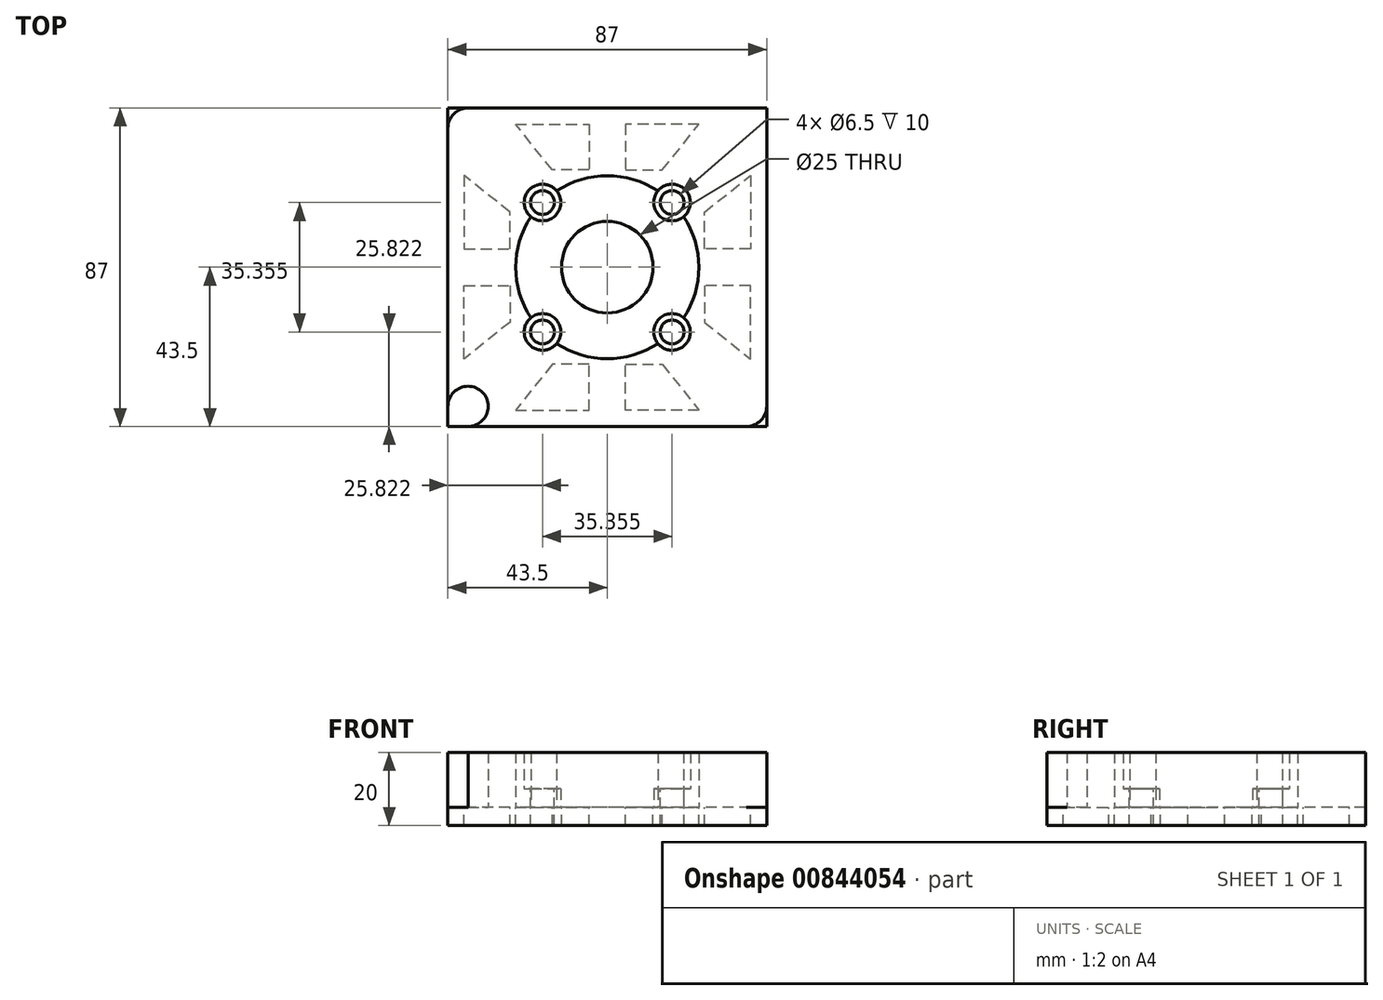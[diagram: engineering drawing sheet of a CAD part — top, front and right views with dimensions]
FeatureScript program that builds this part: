
annotation { "Feature Type Name" : "Feature", "Feature Type Description" : "" }
export const myFeature = defineFeature(function(context is Context, id is Id, definition is map)
    precondition{}
    {
        {
            var Q0;
            Q0=qCreatedBy(makeId("Top.planeOp"),FACE);
            var sketch = newSketch(context, id + "F0", { "sketchPlane" : qUnion([Q0])});
            skLineSegment(sketch, "E0.bottom", {"start": v(-43.5, 43.5) * mm, "end": v(43.5, 43.5) * mm});
            skLineSegment(sketch, "E0.top", {"start": v(-43.5, -43.5) * mm, "end": v(43.5, -43.5) * mm});
            skLineSegment(sketch, "E0.left", {"start": v(-43.5, 43.5) * mm, "end": v(-43.5, -43.5) * mm});
            skLineSegment(sketch, "E0.right", {"start": v(43.5, 43.5) * mm, "end": v(43.5, -43.5) * mm});
            skPoint(sketch, "E0.middle", {"position": v(0, 0) * mm});
            skSolve(sketch);
        }
        {
            var Q0;
            Q0=makeQuery(id+"F0.imprint","IMPRINT",FACE,{"disambiguationData":[TD([[makeQuery(id+"F0.imprint","IMPRINT",EDGE,{"derivedFrom":sQuery(id+"F0.wireOp",EDGE,"E0.bottom")}),-1.0]])]});
            extrude(context, id + "F1", {"entities" : qUnion([Q0]), "depth" : 5 * mm, "offsetDistance" : 25 * mm});
        }
        {
            var Q0;
            Q0=makeQuery(id+"F1.opExtrude","CAP_FACE",FACE,{"disambiguationData":[OSD([sQuery(id+"F0.wireOp",EDGE,"E0.bottom"),sQuery(id+"F0.wireOp",EDGE,"E0.top"),sQuery(id+"F0.wireOp",EDGE,"E0.left"),sQuery(id+"F0.wireOp",EDGE,"E0.right")])],"isStart":false});
            var sketch = newSketch(context, id + "F2", { "sketchPlane" : qUnion([Q0])});
            skCircle(sketch, "E1", {"center": v(0, 0) * mm, "radius": 25 * mm});
            skLineSegment(sketch, "E2", {"start": v(0, 0) * mm, "end": v(-17.68, 17.68) * mm});
            skLineSegment(sketch, "E3", {"start": v(0, 0) * mm, "end": v(17.68, 17.68) * mm});
            skLineSegment(sketch, "E4", {"start": v(0, 0) * mm, "end": v(17.68, -17.68) * mm});
            skLineSegment(sketch, "E5", {"start": v(0, 0) * mm, "end": v(-17.68, -17.68) * mm});
            skPoint(sketch, "E6", {"position": v(-17.68, 17.68) * mm});
            skPoint(sketch, "E7", {"position": v(-17.68, -17.68) * mm});
            skPoint(sketch, "E8", {"position": v(17.68, -17.68) * mm});
            skPoint(sketch, "E9", {"position": v(17.68, 17.68) * mm});
            skCircle(sketch, "E10", {"center": v(-17.68, 17.68) * mm, "radius": 5 * mm});
            skCircle(sketch, "E11", {"center": v(17.68, 17.68) * mm, "radius": 5 * mm});
            skCircle(sketch, "E12", {"center": v(17.68, -17.68) * mm, "radius": 5 * mm});
            skCircle(sketch, "E13", {"center": v(-17.68, -17.68) * mm, "radius": 5 * mm});
            skSolve(sketch);
        }
        {
            var Q0;
            {var subQ0=sQuery(id+"F2.wireOp",EDGE,"E1");var subQ1=makeQuery(id+"F2.imprint","INTERSECT",VERTEX,{"derivedFrom":[subQ0,sQuery(id+"F2.wireOp",EDGE,"E2")]});Q0=makeQuery(id+"F2.imprint","IMPRINT",FACE,{"disambiguationData":[TD([[makeQuery(id+"F2.imprint","IMPRINT",EDGE,{"disambiguationData":[TD([[subQ1,1.0]])],"derivedFrom":subQ0}),-1.0]])]});}
            var Q1;
            {var subQ0=sQuery(id+"F2.wireOp",EDGE,"E2");var subQ1=sQuery(id+"F2.wireOp",EDGE,"E1");var subQ2=makeQuery(id+"F2.imprint","INTERSECT",VERTEX,{"derivedFrom":[subQ1,subQ0]});Q1=makeQuery(id+"F2.imprint","IMPRINT",FACE,{"disambiguationData":[TD([[makeQuery(id+"F2.imprint","IMPRINT",EDGE,{"disambiguationData":[TD([[subQ2,1.0]])],"derivedFrom":subQ1}),1.0]])]});}
            var Q2;
            {var subQ0=sQuery(id+"F2.wireOp",EDGE,"E2");var subQ1=sQuery(id+"F2.wireOp",EDGE,"E1");var subQ2=makeQuery(id+"F2.imprint","INTERSECT",VERTEX,{"derivedFrom":[subQ1,subQ0]});Q2=makeQuery(id+"F2.imprint","IMPRINT",FACE,{"disambiguationData":[TD([[makeQuery(id+"F2.imprint","IMPRINT",EDGE,{"disambiguationData":[TD([[subQ2,-1.0]])],"derivedFrom":subQ1}),1.0]])]});}
            var Q3;
            {var subQ0=sQuery(id+"F2.wireOp",EDGE,"E5");var subQ1=sQuery(id+"F2.wireOp",EDGE,"E1");var subQ2=makeQuery(id+"F2.imprint","INTERSECT",VERTEX,{"derivedFrom":[subQ1,subQ0]});Q3=makeQuery(id+"F2.imprint","IMPRINT",FACE,{"disambiguationData":[TD([[makeQuery(id+"F2.imprint","IMPRINT",EDGE,{"disambiguationData":[TD([[subQ2,1.0]])],"derivedFrom":subQ1}),1.0]])]});}
            var Q4;
            {var subQ0=sQuery(id+"F2.wireOp",EDGE,"E5");var subQ1=sQuery(id+"F2.wireOp",EDGE,"E1");var subQ2=makeQuery(id+"F2.imprint","INTERSECT",VERTEX,{"derivedFrom":[subQ1,subQ0]});Q4=makeQuery(id+"F2.imprint","IMPRINT",FACE,{"disambiguationData":[TD([[makeQuery(id+"F2.imprint","IMPRINT",EDGE,{"disambiguationData":[TD([[subQ2,-1.0]])],"derivedFrom":subQ1}),1.0]])]});}
            var Q5;
            {var subQ0=sQuery(id+"F2.wireOp",EDGE,"E1");var subQ1=makeQuery(id+"F2.imprint","INTERSECT",VERTEX,{"derivedFrom":[subQ0,sQuery(id+"F2.wireOp",EDGE,"E5")]});Q5=makeQuery(id+"F2.imprint","IMPRINT",FACE,{"disambiguationData":[TD([[makeQuery(id+"F2.imprint","IMPRINT",EDGE,{"disambiguationData":[TD([[subQ1,1.0]])],"derivedFrom":subQ0}),-1.0]])]});}
            var Q6;
            {var subQ0=sQuery(id+"F2.wireOp",EDGE,"E4");var subQ1=sQuery(id+"F2.wireOp",EDGE,"E1");var subQ2=makeQuery(id+"F2.imprint","INTERSECT",VERTEX,{"derivedFrom":[subQ1,subQ0]});Q6=makeQuery(id+"F2.imprint","IMPRINT",FACE,{"disambiguationData":[TD([[makeQuery(id+"F2.imprint","IMPRINT",EDGE,{"disambiguationData":[TD([[subQ2,-1.0]])],"derivedFrom":subQ1}),1.0]])]});}
            var Q7;
            {var subQ0=sQuery(id+"F2.wireOp",EDGE,"E4");var subQ1=sQuery(id+"F2.wireOp",EDGE,"E1");var subQ2=makeQuery(id+"F2.imprint","INTERSECT",VERTEX,{"derivedFrom":[subQ1,subQ0]});Q7=makeQuery(id+"F2.imprint","IMPRINT",FACE,{"disambiguationData":[TD([[makeQuery(id+"F2.imprint","IMPRINT",EDGE,{"disambiguationData":[TD([[subQ2,1.0]])],"derivedFrom":subQ1}),1.0]])]});}
            var Q8;
            {var subQ0=sQuery(id+"F2.wireOp",EDGE,"E1");var subQ1=makeQuery(id+"F2.imprint","INTERSECT",VERTEX,{"derivedFrom":[subQ0,sQuery(id+"F2.wireOp",EDGE,"E4")]});Q8=makeQuery(id+"F2.imprint","IMPRINT",FACE,{"disambiguationData":[TD([[makeQuery(id+"F2.imprint","IMPRINT",EDGE,{"disambiguationData":[TD([[subQ1,1.0]])],"derivedFrom":subQ0}),-1.0]])]});}
            var Q9;
            {var subQ0=sQuery(id+"F2.wireOp",EDGE,"E1");var subQ1=makeQuery(id+"F2.imprint","INTERSECT",VERTEX,{"derivedFrom":[subQ0,sQuery(id+"F2.wireOp",EDGE,"E3")]});Q9=makeQuery(id+"F2.imprint","IMPRINT",FACE,{"disambiguationData":[TD([[makeQuery(id+"F2.imprint","IMPRINT",EDGE,{"disambiguationData":[TD([[subQ1,1.0]])],"derivedFrom":subQ0}),-1.0]])]});}
            var Q10;
            {var subQ0=sQuery(id+"F2.wireOp",EDGE,"E3");var subQ1=sQuery(id+"F2.wireOp",EDGE,"E1");var subQ2=makeQuery(id+"F2.imprint","INTERSECT",VERTEX,{"derivedFrom":[subQ1,subQ0]});Q10=makeQuery(id+"F2.imprint","IMPRINT",FACE,{"disambiguationData":[TD([[makeQuery(id+"F2.imprint","IMPRINT",EDGE,{"disambiguationData":[TD([[subQ2,-1.0]])],"derivedFrom":subQ1}),1.0]])]});}
            var Q11;
            {var subQ0=sQuery(id+"F2.wireOp",EDGE,"E3");var subQ1=sQuery(id+"F2.wireOp",EDGE,"E1");var subQ2=makeQuery(id+"F2.imprint","INTERSECT",VERTEX,{"derivedFrom":[subQ1,subQ0]});Q11=makeQuery(id+"F2.imprint","IMPRINT",FACE,{"disambiguationData":[TD([[makeQuery(id+"F2.imprint","IMPRINT",EDGE,{"disambiguationData":[TD([[subQ2,1.0]])],"derivedFrom":subQ1}),1.0]])]});}
            extrude(context, id + "F3", {"entities" : qUnion([Q0, Q1, Q2, Q3, Q4, Q5, Q6, Q7, Q8, Q9, Q10, Q11]), "operationType" : NewBodyOperationType.ADD, "depth" : 5 * mm, "offsetDistance" : 25 * mm});
        }
        {
            var Q0;
            Q0=makeQuery(id+"F2.imprint","IMPRINT",FACE,{"disambiguationData":[TD([[makeQuery(id+"F2.imprint","IMPRINT",EDGE,{"derivedFrom":makeQuery(id+"F1.opExtrude","CAP_EDGE",EDGE,{"disambiguationData":[OSD([sQuery(id+"F0.wireOp",EDGE,"E0.bottom")])],"isStart":false})}),-1.0]])]});
            cPlane(context, id + "F4", {"entities" : qUnion([Q0]), "cplaneType" : CPlaneType.OFFSET, "offset" : 5 * mm, "width" : 150 * mm, "height" : 150 * mm});
        }
        {
            var Q0;
            Q0=qCreatedBy(id+"F4.planeOp",FACE);
            var sketch = newSketch(context, id + "F5", { "sketchPlane" : qUnion([Q0])});
            skCircle(sketch, "E14", {"center": v(0, 0) * mm, "radius": 25 * mm});
            skLineSegment(sketch, "E15", {"start": v(0, 0) * mm, "end": v(-17.68, 17.68) * mm});
            skLineSegment(sketch, "E16", {"start": v(0, 0) * mm, "end": v(17.68, 17.68) * mm});
            skLineSegment(sketch, "E17", {"start": v(0, 0) * mm, "end": v(17.68, -17.68) * mm});
            skLineSegment(sketch, "E18", {"start": v(0, 0) * mm, "end": v(-17.68, -17.68) * mm});
            skPoint(sketch, "E19", {"position": v(-17.68, 17.68) * mm});
            skPoint(sketch, "E20", {"position": v(-17.68, -17.68) * mm});
            skPoint(sketch, "E21", {"position": v(17.68, -17.68) * mm});
            skPoint(sketch, "E22", {"position": v(17.68, 17.68) * mm});
            skCircle(sketch, "E23", {"center": v(-17.68, 17.68) * mm, "radius": 5 * mm});
            skCircle(sketch, "E24", {"center": v(17.68, 17.68) * mm, "radius": 5 * mm});
            skCircle(sketch, "E25", {"center": v(17.68, -17.68) * mm, "radius": 5 * mm});
            skCircle(sketch, "E26", {"center": v(-17.68, -17.68) * mm, "radius": 5 * mm});
            skSolve(sketch);
        }
        {
            var Q0;
            Q0=sQuery(id+"F5.wireOp",VERTEX,"E19");
            var Q1;
            Q1=sQuery(id+"F5.wireOp",VERTEX,"E22");
            var Q2;
            Q2=sQuery(id+"F5.wireOp",VERTEX,"E21");
            var Q3;
            Q3=sQuery(id+"F5.wireOp",VERTEX,"E20");
            var Q4;
            Q4=makeQuery(id+"F1.opExtrude","SWEPT_BODY",BODY,{"disambiguationData":[OSD([sQuery(id+"F0.wireOp",EDGE,"E0.bottom"),sQuery(id+"F0.wireOp",EDGE,"E0.top"),sQuery(id+"F0.wireOp",EDGE,"E0.left"),sQuery(id+"F0.wireOp",EDGE,"E0.right")])]});
            hole(context, id + "F6", {"style" : HoleStyle.SIMPLE, "endStyle" : HoleEndStyle.THROUGH, "holeDiameter" : 6.5 * mm, "majorDiameter" : 5 * mm, "isTappedThrough" : true, "tappedDepth" : 12 * mm, "tapClearance" : 3, "locations" : qUnion([Q0, Q1, Q2, Q3]), "scope" : qUnion([Q4])});
        }
        {
            var Q0;
            Q0=makeQuery(id+"F2.imprint","IMPRINT",FACE,{"disambiguationData":[TD([[makeQuery(id+"F2.imprint","IMPRINT",EDGE,{"derivedFrom":makeQuery(id+"F1.opExtrude","CAP_EDGE",EDGE,{"disambiguationData":[OSD([sQuery(id+"F0.wireOp",EDGE,"E0.bottom")])],"isStart":false})}),-1.0]])]});
            var sketch = newSketch(context, id + "F7", { "sketchPlane" : qUnion([Q0])});
            skCircle(sketch, "E27", {"center": v(-38, 38) * mm, "radius": 5.5 * mm});
            skCircle(sketch, "E28.MirrorC", {"center": v(-38, -38) * mm, "radius": 5.5 * mm});
            skCircle(sketch, "E29.MirrorC", {"center": v(38, -38) * mm, "radius": 5.5 * mm});
            skSolve(sketch);
        }
        {
            var Q0;
            {var subQ0=sQuery(id+"F7.wireOp",EDGE,"E27");var subQ1=makeQuery(id+"F7.imprint","INTERSECT",VERTEX,{"derivedFrom":[makeQuery(id+"F2.imprint","IMPRINT",EDGE,{"derivedFrom":makeQuery(id+"F1.opExtrude","CAP_EDGE",EDGE,{"disambiguationData":[OSD([sQuery(id+"F0.wireOp",EDGE,"E0.bottom")])],"isStart":false})}),subQ0]});Q0=makeQuery(id+"F7.imprint","IMPRINT",FACE,{"disambiguationData":[TD([[makeQuery(id+"F7.imprint","IMPRINT",EDGE,{"disambiguationData":[TD([[subQ1,-1.0]])],"derivedFrom":subQ0}),1.0]])]});}
            var Q1;
            {var subQ0=sQuery(id+"F7.wireOp",EDGE,"E28.MirrorC");var subQ1=makeQuery(id+"F7.imprint","INTERSECT",VERTEX,{"derivedFrom":[makeQuery(id+"F2.imprint","IMPRINT",EDGE,{"derivedFrom":makeQuery(id+"F1.opExtrude","CAP_EDGE",EDGE,{"disambiguationData":[OSD([sQuery(id+"F0.wireOp",EDGE,"E0.top")])],"isStart":false})}),subQ0]});Q1=makeQuery(id+"F7.imprint","IMPRINT",FACE,{"disambiguationData":[TD([[makeQuery(id+"F7.imprint","IMPRINT",EDGE,{"disambiguationData":[TD([[subQ1,-1.0]])],"derivedFrom":subQ0}),-1.0]])]});}
            var Q2;
            {var subQ0=sQuery(id+"F7.wireOp",EDGE,"E29.MirrorC");var subQ1=makeQuery(id+"F7.imprint","INTERSECT",VERTEX,{"derivedFrom":[makeQuery(id+"F2.imprint","IMPRINT",EDGE,{"derivedFrom":makeQuery(id+"F1.opExtrude","CAP_EDGE",EDGE,{"disambiguationData":[OSD([sQuery(id+"F0.wireOp",EDGE,"E0.top")])],"isStart":false})}),subQ0]});Q2=makeQuery(id+"F7.imprint","IMPRINT",FACE,{"disambiguationData":[TD([[makeQuery(id+"F7.imprint","IMPRINT",EDGE,{"disambiguationData":[TD([[subQ1,-1.0]])],"derivedFrom":subQ0}),1.0]])]});}
            extrude(context, id + "F8", {"entities" : qUnion([Q0, Q1, Q2]), "operationType" : NewBodyOperationType.ADD, "depth" : 15 * mm, "offsetDistance" : 25 * mm});
        }
        {
            var Q0;
            Q0=makeQuery(id+"F2.imprint","IMPRINT",FACE,{"disambiguationData":[TD([[makeQuery(id+"F2.imprint","IMPRINT",EDGE,{"derivedFrom":makeQuery(id+"F1.opExtrude","CAP_EDGE",EDGE,{"disambiguationData":[OSD([sQuery(id+"F0.wireOp",EDGE,"E0.bottom")])],"isStart":false})}),-1.0]])]});
            var sketch = newSketch(context, id + "F9", { "sketchPlane" : qUnion([Q0])});
            skLineSegment(sketch, "E30", {"start": v(5.01, 26.55) * mm, "end": v(15.03, 26.55) * mm});
            skLineSegment(sketch, "E31", {"start": v(15.03, 26.55) * mm, "end": v(25.05, 39.08) * mm});
            skLineSegment(sketch, "E32", {"start": v(25.05, 39.08) * mm, "end": v(5.01, 39.08) * mm});
            skLineSegment(sketch, "E33", {"start": v(5.01, 39.08) * mm, "end": v(5.01, 26.55) * mm});
            skLineSegment(sketch, "E34.MirrorCS", {"start": v(-25.05, 39.08) * mm, "end": v(-5.01, 39.08) * mm});
            skLineSegment(sketch, "E35.MirrorCS", {"start": v(-5.01, 39.08) * mm, "end": v(-5.01, 26.55) * mm});
            skLineSegment(sketch, "E36.MirrorCS", {"start": v(-5.01, 26.55) * mm, "end": v(-15.03, 26.55) * mm});
            skLineSegment(sketch, "E37.MirrorCS", {"start": v(-15.03, 26.55) * mm, "end": v(-25.05, 39.08) * mm});
            skLineSegment(sketch, "E38.MirrorCS", {"start": v(26.55, 5.01) * mm, "end": v(26.55, 15.03) * mm});
            skLineSegment(sketch, "E39.MirrorCS", {"start": v(39.08, 5.01) * mm, "end": v(26.55, 5.01) * mm});
            skLineSegment(sketch, "E40.MirrorCS", {"start": v(39.08, 25.05) * mm, "end": v(39.08, 5.01) * mm});
            skLineSegment(sketch, "E41.MirrorCS", {"start": v(26.55, 15.03) * mm, "end": v(39.08, 25.05) * mm});
            skLineSegment(sketch, "E42.MirrorCS", {"start": v(26.55, -5.01) * mm, "end": v(26.55, -15.03) * mm});
            skLineSegment(sketch, "E43.MirrorCS", {"start": v(39.08, -5.01) * mm, "end": v(26.55, -5.01) * mm});
            skLineSegment(sketch, "E44.MirrorCS", {"start": v(39.08, -25.05) * mm, "end": v(39.08, -5.01) * mm});
            skLineSegment(sketch, "E45.MirrorCS", {"start": v(26.55, -15.03) * mm, "end": v(39.08, -25.05) * mm});
            skLineSegment(sketch, "E46.MirrorCS", {"start": v(-25.05, -39.08) * mm, "end": v(-5.01, -39.08) * mm});
            skLineSegment(sketch, "E47.MirrorCS", {"start": v(-5.01, -39.08) * mm, "end": v(-5.01, -26.55) * mm});
            skLineSegment(sketch, "E48.MirrorCS", {"start": v(5.01, -39.08) * mm, "end": v(5.01, -26.55) * mm});
            skLineSegment(sketch, "E49.MirrorCS", {"start": v(-15.03, -26.55) * mm, "end": v(-25.05, -39.08) * mm});
            skLineSegment(sketch, "E50.MirrorCS", {"start": v(25.05, -39.08) * mm, "end": v(5.01, -39.08) * mm});
            skLineSegment(sketch, "E51.MirrorCS", {"start": v(5.01, -26.55) * mm, "end": v(15.03, -26.55) * mm});
            skLineSegment(sketch, "E52.MirrorCS", {"start": v(15.03, -26.55) * mm, "end": v(25.05, -39.08) * mm});
            skLineSegment(sketch, "E53.MirrorCS", {"start": v(-5.01, -26.55) * mm, "end": v(-15.03, -26.55) * mm});
            skLineSegment(sketch, "E54.MirrorCS", {"start": v(-26.55, 15.03) * mm, "end": v(-39.08, 25.05) * mm});
            skLineSegment(sketch, "E55.MirrorCS", {"start": v(-39.08, 5.01) * mm, "end": v(-26.55, 5.01) * mm});
            skLineSegment(sketch, "E56.MirrorCS", {"start": v(-39.08, 25.05) * mm, "end": v(-39.08, 5.01) * mm});
            skLineSegment(sketch, "E57.MirrorCS", {"start": v(-26.55, 5.01) * mm, "end": v(-26.55, 15.03) * mm});
            skLineSegment(sketch, "E58.MirrorCS", {"start": v(-39.08, -5.01) * mm, "end": v(-26.55, -5.01) * mm});
            skLineSegment(sketch, "E59.MirrorCS", {"start": v(-26.55, -5.01) * mm, "end": v(-26.55, -15.03) * mm});
            skLineSegment(sketch, "E60.MirrorCS", {"start": v(-39.08, -25.05) * mm, "end": v(-39.08, -5.01) * mm});
            skLineSegment(sketch, "E61.MirrorCS", {"start": v(-26.55, -15.03) * mm, "end": v(-39.08, -25.05) * mm});
            skCircle(sketch, "E62", {"center": v(0, 0) * mm, "radius": 12.5 * mm});
            skSolve(sketch);
        }
        {
            var Q0;
            Q0 = qSketchRegion(id + "F9", true);
            extrude(context, id + "F10", {"entities" : qUnion([Q0]), "operationType" : NewBodyOperationType.REMOVE, "oppositeDirection" : true, "depth" : 5 * mm, "offsetDistance" : 25 * mm});
        }
    });
